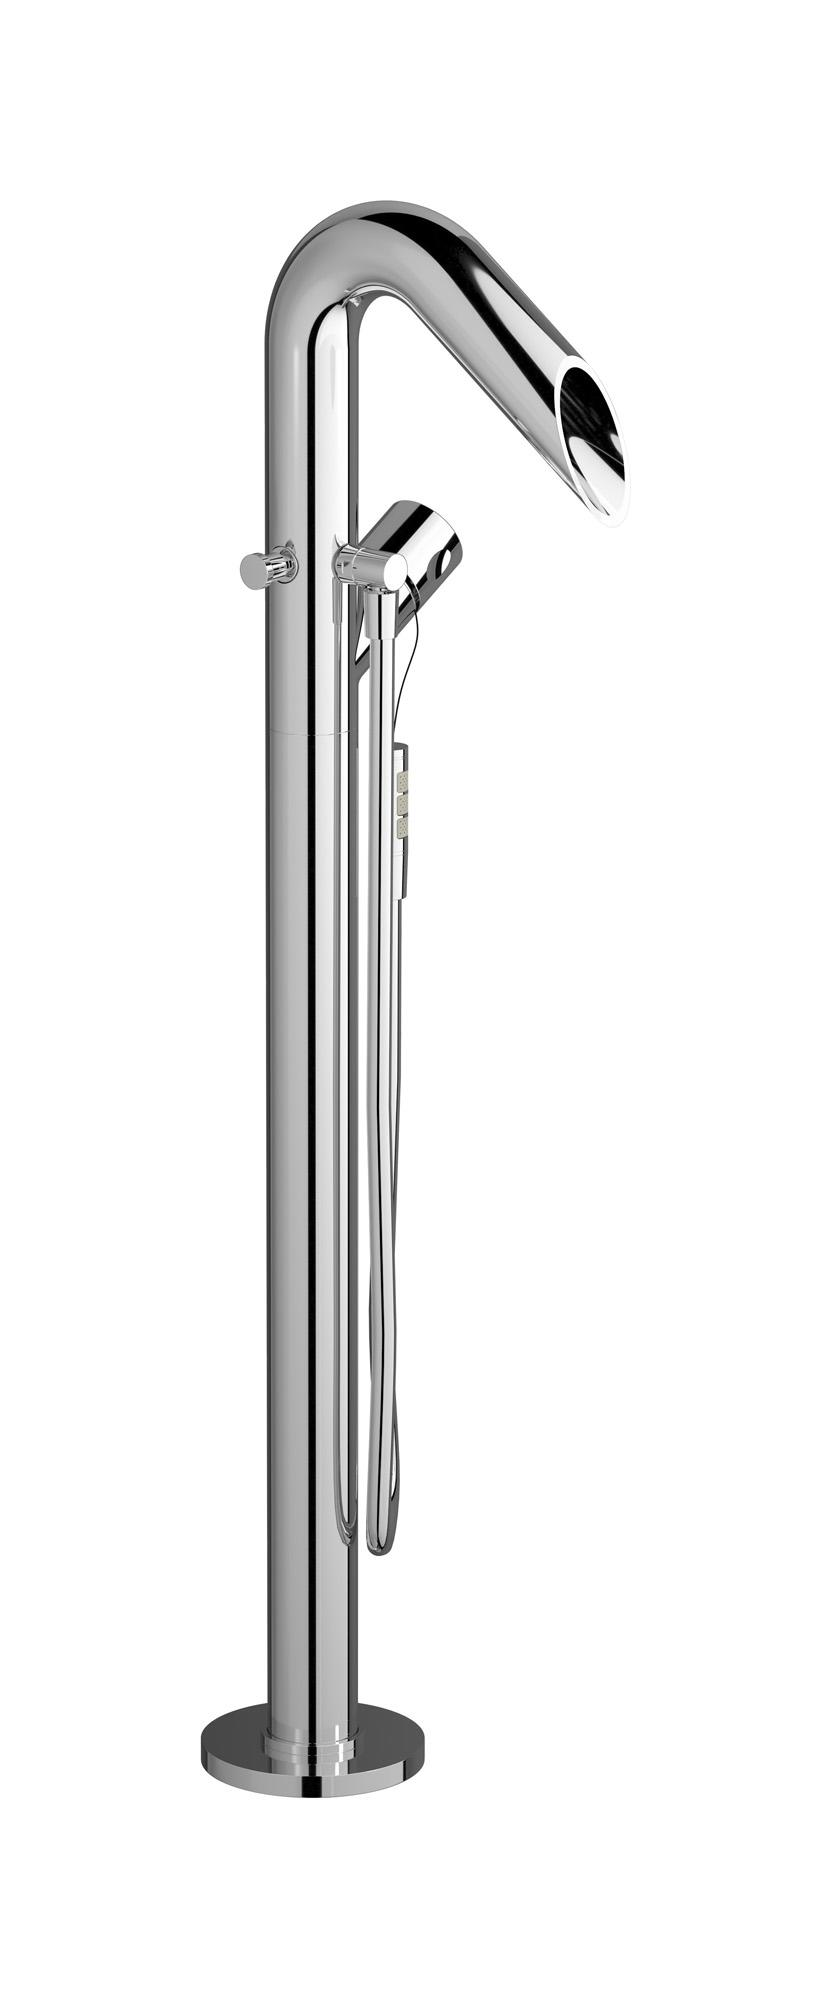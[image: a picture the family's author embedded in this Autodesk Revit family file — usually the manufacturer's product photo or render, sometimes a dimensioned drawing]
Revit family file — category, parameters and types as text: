
# Revit family: OO399
name_source: partatom
category: Apparecchi idraulici
units: mm (PartAtom-declared; Revit-internal decimal feet)

## family parameters
Basato su piano di lavoro = No
Condiviso = No
Mantieni orientamento annotazione = No
Numero OmniClass = 23.45.55.17
Punto di calcolo locali = No
Quota connettore circolare = Usa diametro
Sempre verticale = Sì
Taglio con vuoti quando caricato = No
Tipo di parte = Normale
Titolo OmniClass = Mixing Faucets

## types (1)
- Chrome
    Cold water inlet = 10 mm  [stored 0.0328084 ft]
    Commenti sul tipo = Bath filler
    Connessione CW = No
    Connessione HW = No
    Connessione di scarico = No
    Connessione di ventilazione = No
    Descrizione = Freestanding bath filler
    Finishes surface = IB_Chrome
    Hot water inlet = 10 mm  [stored 0.0328084 ft]
    Immagine tipo = OO399CC.jpg
    Modello = OO399CC
    Produttore = IB Rubinetterie S.p.A.
    Prospetto di default = 0 mm  [stored 0 ft]
    URL = https://www.weareib.it

note: [stored X ft] marks values corroborated as IEEE doubles in the binary element streams (Revit-internal decimal feet)
